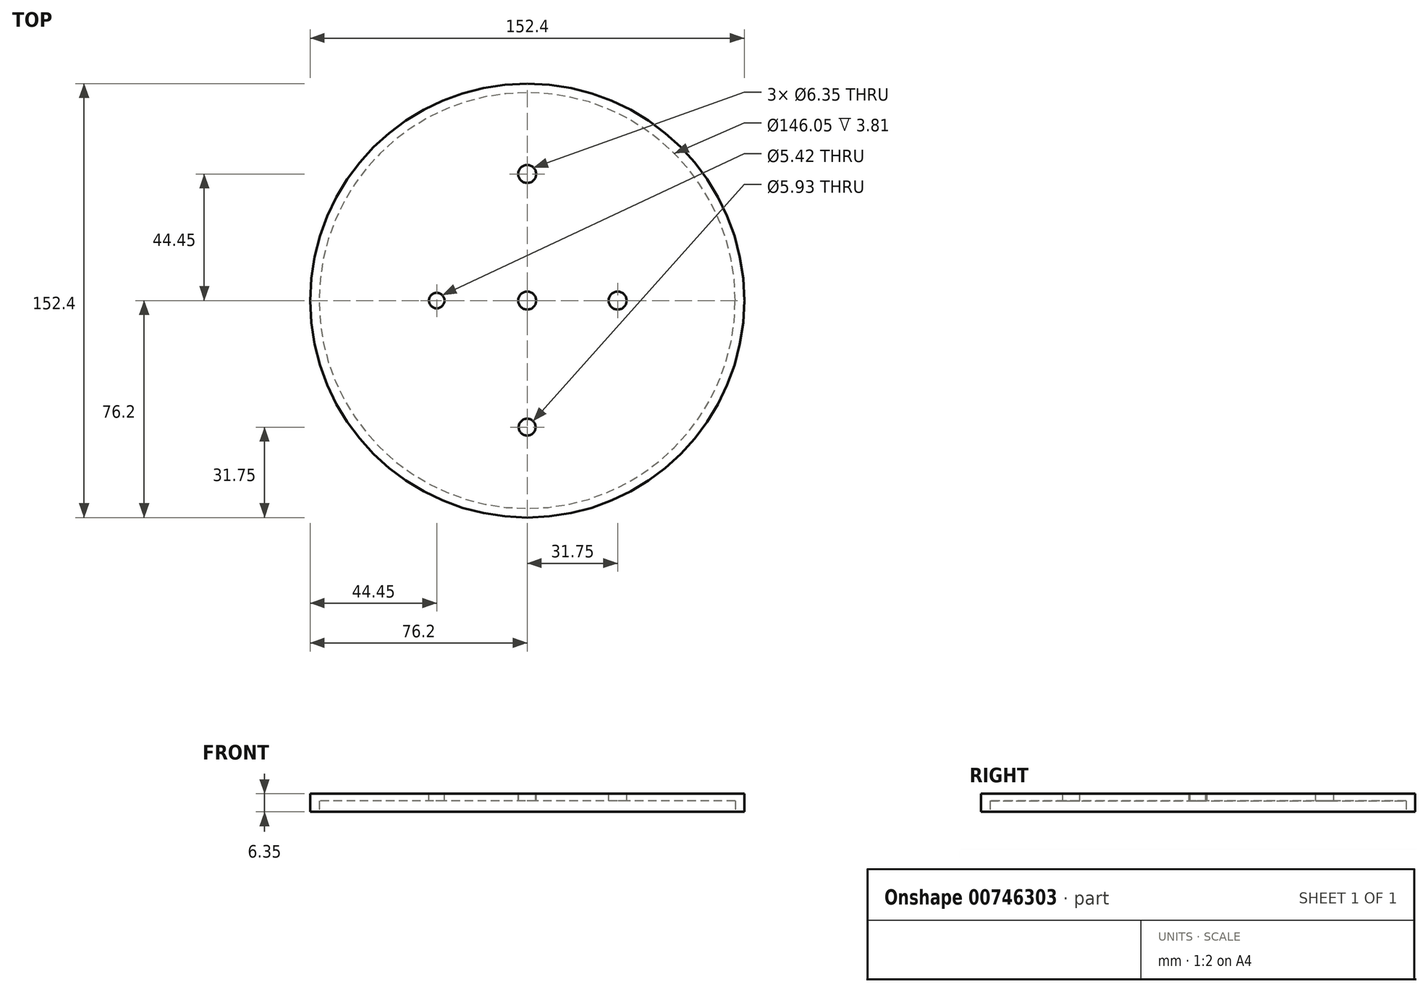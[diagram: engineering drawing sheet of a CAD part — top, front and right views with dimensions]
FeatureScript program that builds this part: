
annotation { "Feature Type Name" : "Feature", "Feature Type Description" : "" }
export const myFeature = defineFeature(function(context is Context, id is Id, definition is map)
    precondition{}
    {
        {
            var Q0;
            Q0=qCreatedBy(makeId("Top.planeOp"),FACE);
            var sketch = newSketch(context, id + "F0", { "sketchPlane" : qUnion([Q0])});
            skCircle(sketch, "E0", {"center": v(0, 0) * mm, "radius": 76.2 * mm});
            skSolve(sketch);
        }
        {
            var Q0;
            Q0 = qSketchRegion(id + "F0", true);
            extrude(context, id + "F1", {"entities" : qUnion([Q0]), "depth" : 6.35 * mm, "offsetDistance" : 25.4 * mm});
        }
        {
            var Q0;
            Q0=qCreatedBy(makeId("Top.planeOp"),FACE);
            var sketch = newSketch(context, id + "F2", { "sketchPlane" : qUnion([Q0])});
            skCircle(sketch, "E1", {"center": v(0, 0) * mm, "radius": 73.02 * mm});
            skSolve(sketch);
        }
        {
            var Q0;
            Q0=makeQuery(id+"F2.imprint","IMPRINT",FACE,{"disambiguationData":[TD([[makeQuery(id+"F2.imprint","IMPRINT",EDGE,{"derivedFrom":sQuery(id+"F2.wireOp",EDGE,"E1")}),1.0]])]});
            extrude(context, id + "F3", {"entities" : qUnion([Q0]), "operationType" : NewBodyOperationType.REMOVE, "depth" : 3.8 * mm, "offsetDistance" : 25.4 * mm});
        }
        {
            var Q0;
            Q0=makeQuery(id+"F1.opExtrude","CAP_FACE",FACE,{"disambiguationData":[OSD([sQuery(id+"F0.wireOp",EDGE,"E0")])],"isStart":false});
            var sketch = newSketch(context, id + "F4", { "sketchPlane" : qUnion([Q0])});
            skCircle(sketch, "E2", {"center": v(-31.75, 0) * mm, "radius": 2.71 * mm});
            skCircle(sketch, "E3", {"center": v(31.75, 0) * mm, "radius": 3.18 * mm});
            skCircle(sketch, "E4", {"center": v(0, 0) * mm, "radius": 3.18 * mm});
            skSolve(sketch);
        }
        {
            var Q0;
            Q0 = qSketchRegion(id + "F4", true);
            extrude(context, id + "F5", {"entities" : qUnion([Q0]), "operationType" : NewBodyOperationType.REMOVE, "endBound" : BoundingType.THROUGH_ALL, "oppositeDirection" : true, "depth" : 25.4 * mm, "offsetDistance" : 25.4 * mm});
        }
        {
            var Q0;
            Q0=makeQuery(id+"F1.opExtrude","CAP_FACE",FACE,{"disambiguationData":[OSD([sQuery(id+"F0.wireOp",EDGE,"E0")])],"isStart":false});
            var sketch = newSketch(context, id + "F6", { "sketchPlane" : qUnion([Q0])});
            skCircle(sketch, "E5", {"center": v(0, 44.45) * mm, "radius": 3.18 * mm});
            skCircle(sketch, "E6", {"center": v(0, -44.45) * mm, "radius": 2.97 * mm});
            skSolve(sketch);
        }
        {
            var Q0;
            Q0 = qSketchRegion(id + "F6", true);
            extrude(context, id + "F7", {"entities" : qUnion([Q0]), "operationType" : NewBodyOperationType.REMOVE, "endBound" : BoundingType.THROUGH_ALL, "oppositeDirection" : true, "depth" : 25.4 * mm, "offsetDistance" : 25.4 * mm});
        }
    });
